# Revit family: AISC S Shapes-Section
name_source: partatom
category: Detail Items
revit_build: Autodesk Revit Architecture 2012 (Build: 20110210_1515)
units: mm (PartAtom-declared; Revit-internal decimal feet)

## types (28) — shared parameters
Keynote = 05 12 00.I0

## per-type parameters (varying)
| type | A | W | bf | d | k | r | tf | tw |
| S24X121 | 0.25 SF | 121 | 0' - 8 1/16" | 2' - 0 1/2" | 0' - 2" | 0' - 0 29/32" | 0' - 1 3/32" | 0' - 0 13/16" |
| S24X106 | 0.22 SF | 106 | 0' - 7 7/8" | 2' - 0 1/2" | 0' - 2" | 0' - 0 29/32" | 0' - 1 3/32" | 0' - 0 5/8" |
| S24X100 | 0.2 SF | 100 | 0' - 7 1/4" | 2' - 0" | 0' - 1 3/4" | 0' - 0 7/8" | 0' - 0 7/8" | 0' - 0 3/4" |
| S24X90 | 0.18 SF | 90 | 0' - 7 1/8" | 2' - 0" | 0' - 1 3/4" | 0' - 0 7/8" | 0' - 0 7/8" | 0' - 0 5/8" |
| S24X80 | 0.16 SF | 80 | 0' - 7" | 2' - 0" | 0' - 1 3/4" | 0' - 0 7/8" | 0' - 0 7/8" | 0' - 0 1/2" |
| S20X96 | 0.2 SF | 96 | 0' - 7 3/16" | 1' - 8 5/16" | 0' - 1 3/4" | 0' - 0 27/32" | 0' - 0 29/32" | 0' - 0 13/16" |
| S20X86 | 0.18 SF | 86 | 0' - 7 1/16" | 1' - 8 5/16" | 0' - 1 3/4" | 0' - 0 27/32" | 0' - 0 29/32" | 0' - 0 21/32" |
| S20X75 | 0.15 SF | 75 | 0' - 6 3/8" | 1' - 8" | 0' - 1 5/8" | 0' - 0 27/32" | 0' - 0 25/32" | 0' - 0 5/8" |
| S20X66 | 0.13 SF | 66 | 0' - 6 1/4" | 1' - 8" | 0' - 1 5/8" | 0' - 0 27/32" | 0' - 0 25/32" | 0' - 0 1/2" |
| S18X70 | 0.14 SF | 70 | 0' - 6 1/4" | 1' - 6" | 0' - 1 1/2" | 0' - 0 13/16" | 0' - 0 11/16" | 0' - 0 23/32" |
| S18X54.7 | 0.11 SF | 54.7 | 0' - 6" | 1' - 6" | 0' - 1 1/2" | 0' - 0 13/16" | 0' - 0 11/16" | 0' - 0 15/32" |
| S15X50 | 0.1 SF | 50 | 0' - 5 5/8" | 1' - 3" | 0' - 1 3/8" | 0' - 0 3/4" | 0' - 0 5/8" | 0' - 0 9/16" |
| S15X42.9 | 0.09 SF | 42.9 | 0' - 5 1/2" | 1' - 3" | 0' - 1 3/8" | 0' - 0 3/4" | 0' - 0 5/8" | 0' - 0 13/32" |
| S12X50 | 0.1 SF | 50 | 0' - 5 15/32" | 1' - 0" | 0' - 1 7/16" | 0' - 0 25/32" | 0' - 0 21/32" | 0' - 0 11/16" |
| S12X40.8 | 0.08 SF | 40.8 | 0' - 5 1/4" | 1' - 0" | 0' - 1 7/16" | 0' - 0 25/32" | 0' - 0 21/32" | 0' - 0 15/32" |
| S12X35 | 0.07 SF | 35 | 0' - 5 3/32" | 1' - 0" | 0' - 1 3/16" | 0' - 0 21/32" | 0' - 0 17/32" | 0' - 0 7/16" |
| S12X31.8 | 0.06 SF | 31.8 | 0' - 5" | 1' - 0" | 0' - 1 3/16" | 0' - 0 21/32" | 0' - 0 17/32" | 0' - 0 11/32" |
| S10X35 | 0.07 SF | 35 | 0' - 4 15/16" | 0' - 10" | 0' - 1 1/8" | 0' - 0 5/8" | 0' - 0 1/2" | 0' - 0 19/32" |
| S10X25.4 | 0.05 SF | 25.4 | 0' - 4 21/32" | 0' - 10" | 0' - 1 1/8" | 0' - 0 5/8" | 0' - 0 1/2" | 0' - 0 5/16" |
| S8X23 | 0.05 SF | 23 | 0' - 4 5/32" | 0' - 8" | 0' - 1" | 0' - 0 9/16" | 0' - 0 7/16" | 0' - 0 7/16" |
| S8X18.4 | 0.04 SF | 18.4 | 0' - 4" | 0' - 8" | 0' - 1" | 0' - 0 9/16" | 0' - 0 7/16" | 0' - 0 9/32" |
| S6X17.2 | 0.04 SF | 17.3 | 0' - 3 9/16" | 0' - 6" | 0' - 0 13/16" | 0' - 0 15/32" | 0' - 0 11/32" | 0' - 0 15/32" |
| S6X12.5 | 0.03 SF | 12.5 | 0' - 3 11/32" | 0' - 6" | 0' - 0 13/16" | 0' - 0 15/32" | 0' - 0 11/32" | 0' - 0 7/32" |
| S5X10 | 0.02 SF | 10 | 0' - 3" | 0' - 5" | 0' - 0 3/4" | 0' - 0 7/16" | 0' - 0 5/16" | 0' - 0 7/32" |
| S4X9.5 | 0.02 SF | 9.5 | 0' - 2 13/16" | 0' - 4" | 0' - 0 3/4" | 0' - 0 15/32" | 0' - 0 9/32" | 0' - 0 5/16" |
| S4X7.7 | 0.02 SF | 7.7 | 0' - 2 21/32" | 0' - 4" | 0' - 0 3/4" | 0' - 0 15/32" | 0' - 0 9/32" | 0' - 0 3/16" |
| S3X7.5 | 0.02 SF | 7.5 | 0' - 2 1/2" | 0' - 3" | 0' - 0 5/8" | 0' - 0 3/8" | 0' - 0 1/4" | 0' - 0 11/32" |
| S3X5.7 | 0.01 SF | 5.7 | 0' - 2 11/32" | 0' - 3" | 0' - 0 5/8" | 0' - 0 3/8" | 0' - 0 1/4" | 0' - 0 5/32" |
